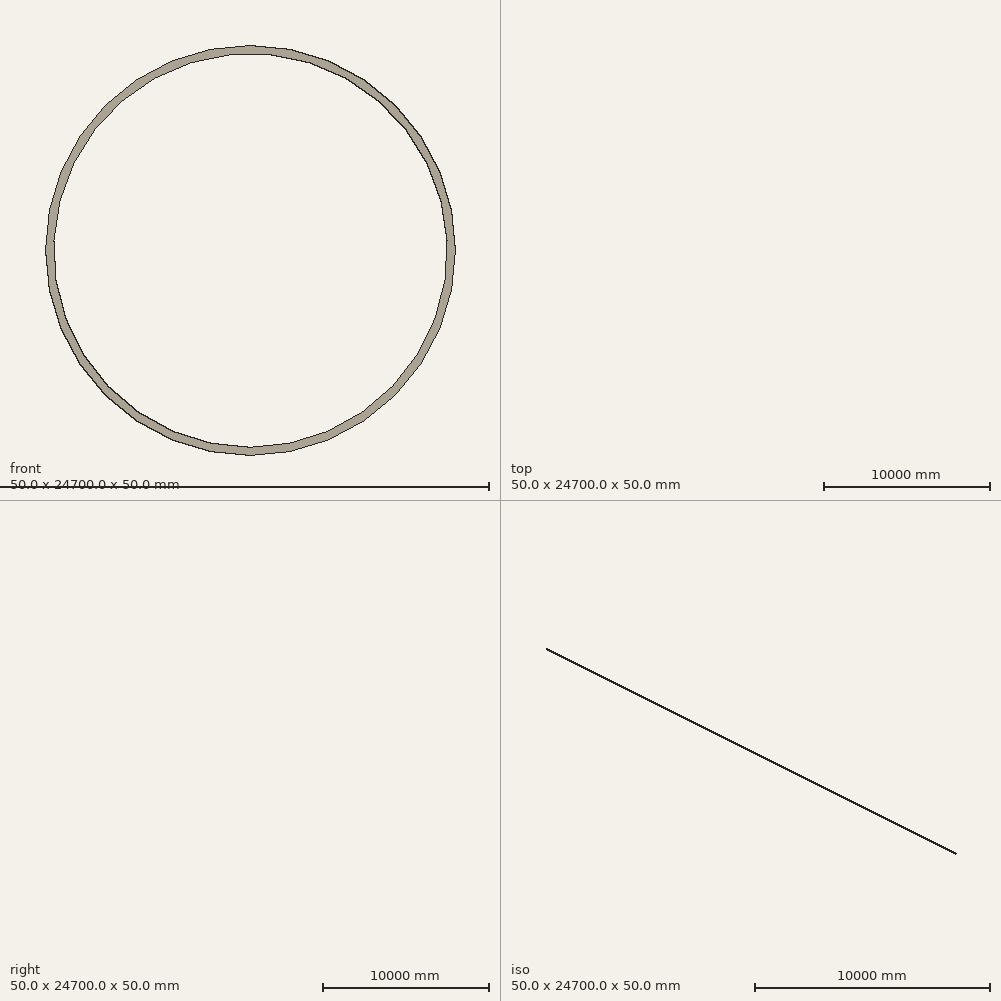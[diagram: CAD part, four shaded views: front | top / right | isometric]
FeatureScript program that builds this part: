
annotation { "Feature Type Name" : "Feature", "Feature Type Description" : "" }
export const myFeature = defineFeature(function(context is Context, id is Id, definition is map)
    precondition{}
    {
        {
            var Q0;
            Q0=qCreatedBy(makeId("Front.planeOp"),FACE);
            var sketch = newSketch(context, id + "F0", { "sketchPlane" : qUnion([Q0])});
            skCircle(sketch, "E0", {"center": v(0, 0) * mm, "radius": 25 * mm});
            skCircle(sketch, "E1", {"center": v(0, 0) * mm, "radius": 24 * mm});
            skSolve(sketch);
        }
        {
            var Q0;
            Q0=qSketchRegion(id+"F0",true);
            extrude(context, id + "F1", {"entities" : qUnion([Q0]), "depth" : 24700 * mm, "offsetDistance" : 25 * mm});
        }
    });
